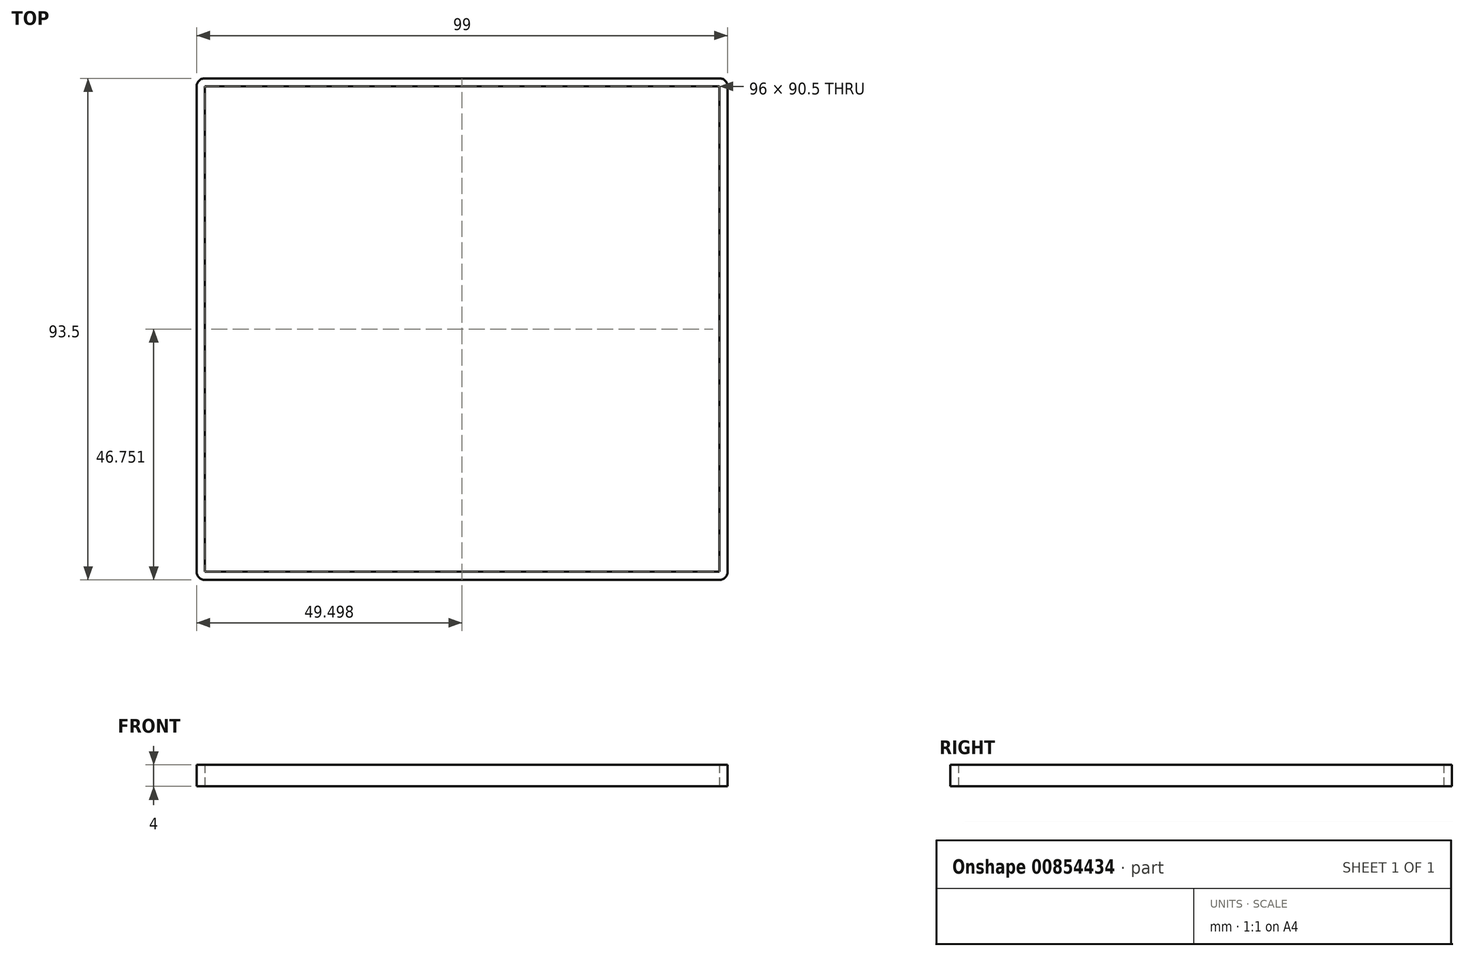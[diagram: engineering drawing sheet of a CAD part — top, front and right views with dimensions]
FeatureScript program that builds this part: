
annotation { "Feature Type Name" : "Feature", "Feature Type Description" : "" }
export const myFeature = defineFeature(function(context is Context, id is Id, definition is map)
    precondition{}
    {
        {
            var Q0;
            Q0=qCreatedBy(makeId("Top.planeOp"),FACE);
            var sketch = newSketch(context, id + "F0", { "sketchPlane" : qUnion([Q0])});
            skLineSegment(sketch, "E0.bottom", {"start": v(-48.57, 40.2) * mm, "end": v(47.43, 40.2) * mm});
            skLineSegment(sketch, "E0.top", {"start": v(-48.57, -53.3) * mm, "end": v(47.43, -53.3) * mm});
            skLineSegment(sketch, "E0.left", {"start": v(-50.07, 38.7) * mm, "end": v(-50.07, -51.8) * mm});
            skLineSegment(sketch, "E0.right", {"start": v(48.93, 38.7) * mm, "end": v(48.93, -51.8) * mm});
            skLineSegment(sketch, "E1.bottom", {"start": v(-48.57, 38.7) * mm, "end": v(47.43, 38.7) * mm});
            skLineSegment(sketch, "E1.top", {"start": v(-48.57, -51.8) * mm, "end": v(47.43, -51.8) * mm});
            skLineSegment(sketch, "E1.left", {"start": v(-48.57, 38.7) * mm, "end": v(-48.57, -51.8) * mm});
            skLineSegment(sketch, "E1.right", {"start": v(47.43, 38.7) * mm, "end": v(47.43, -51.8) * mm});
            skPoint(sketch, "E2.visualSharp", {"position": v(-50.07, 40.2) * mm});
            skArc(sketch, "E2.filletArc", {"start": v(-48.57, 40.2) * mm, "mid": v(-49.63, 39.75) * mm, "end": v(-50.07, 38.7) * mm});
            skPoint(sketch, "E3.visualSharp", {"position": v(48.93, 40.2) * mm});
            skArc(sketch, "E3.filletArc", {"start": v(48.93, 38.7) * mm, "mid": v(48.49, 39.75) * mm, "end": v(47.43, 40.2) * mm});
            skPoint(sketch, "E4.visualSharp", {"position": v(48.93, -53.3) * mm});
            skArc(sketch, "E4.filletArc", {"start": v(47.43, -53.3) * mm, "mid": v(48.49, -52.87) * mm, "end": v(48.93, -51.8) * mm});
            skPoint(sketch, "E5.visualSharp", {"position": v(-50.07, -53.3) * mm});
            skArc(sketch, "E5.filletArc", {"start": v(-50.07, -51.8) * mm, "mid": v(-49.63, -52.87) * mm, "end": v(-48.57, -53.3) * mm});
            skSolve(sketch);
        }
        {
            var Q0;
            Q0=makeQuery(id+"F0.imprint","IMPRINT",FACE,{"disambiguationData":[TD([[makeQuery(id+"F0.imprint","IMPRINT",EDGE,{"derivedFrom":sQuery(id+"F0.wireOp",EDGE,"E0.bottom")}),-1.0]])]});
            extrude(context, id + "F1", {"entities" : qUnion([Q0]), "depth" : 4 * mm, "offsetDistance" : 25 * mm});
        }
    });
